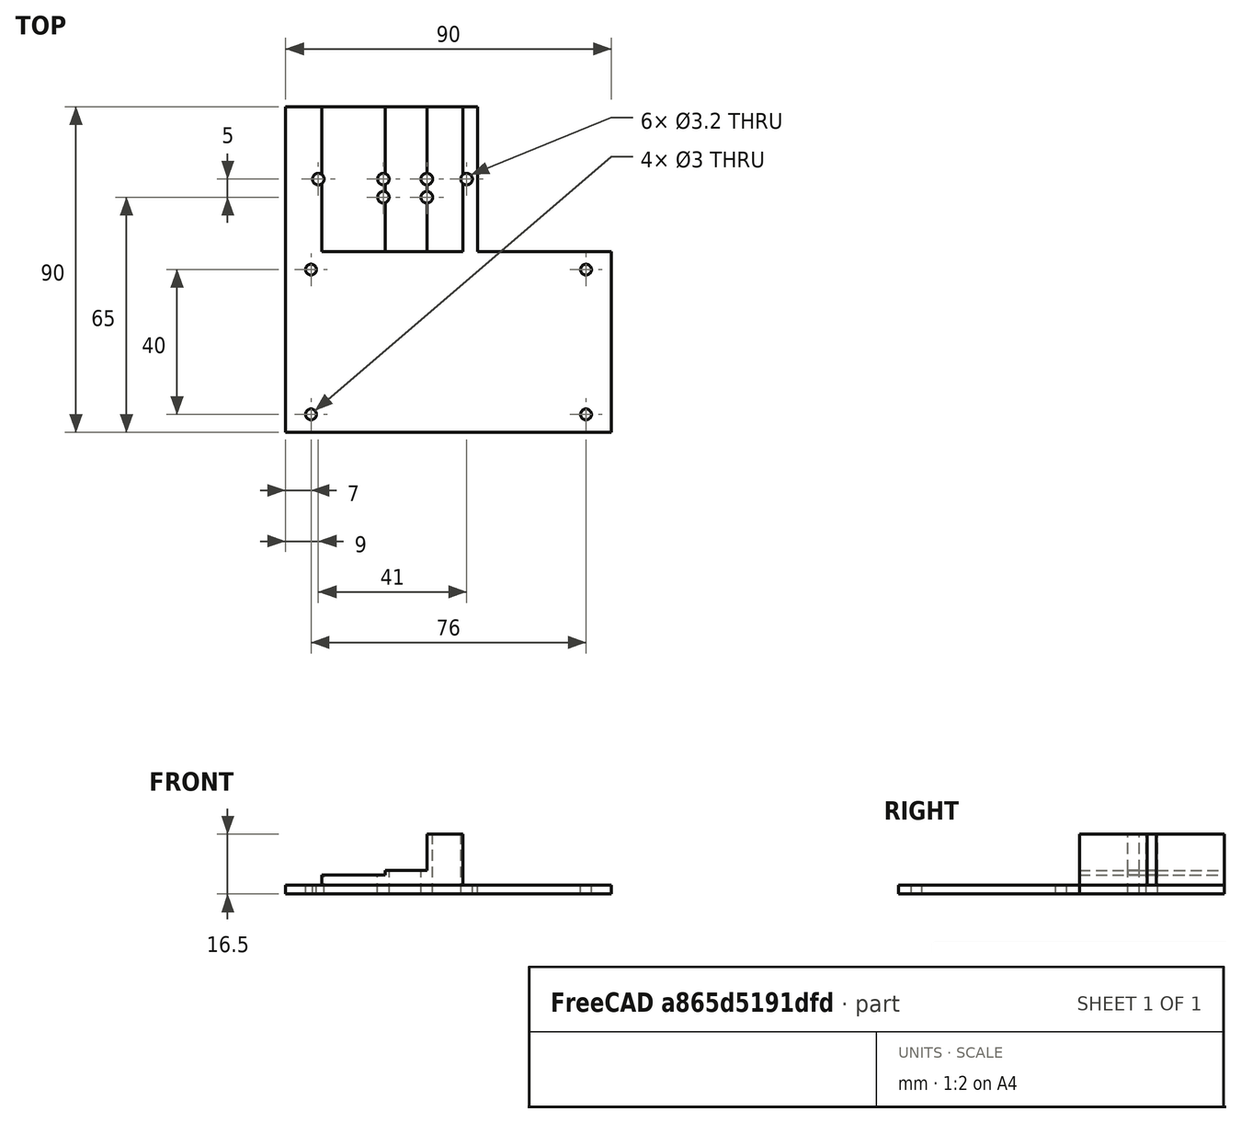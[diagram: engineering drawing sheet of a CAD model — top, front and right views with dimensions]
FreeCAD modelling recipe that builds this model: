
FCSTD DOCUMENT  (FreeCAD 0.16R6707 (Git))
Label: U3-base
License: All rights reserved
LicenseURL: http://en.wikipedia.org/wiki/All_rights_reserved
objects: Part::Cut×11, Part::Cylinder×10, Part::Box×5, Part::MultiFuse×3
note: 29 computed .brp shape members not serialized (recipe doc carries the construction recipe); baked Part::Feature solids carry a one-line shape summary decoded from their .brp

FEATURE [Part::Box] Box  label="Cube"
  Height = 2.5
  Length = 90
  Placement = pos=(0,0,-2.5) rot=(0,0,1;0rad)
  Width = 90
FEATURE [Part::Cylinder] Cylinder
  Angle = 360
  Height = 10
  Placement = pos=(7,5,-5) rot=(0,0,1;0rad)
  Radius = 1.5
FEATURE [Part::Cylinder] Cylinder001
  Angle = 360
  Height = 10
  Placement = pos=(7,45,-5) rot=(0,0,1;0rad)
  Radius = 1.5
FEATURE [Part::Cylinder] Cylinder002
  Angle = 360
  Height = 10
  Placement = pos=(83,5,-5) rot=(0,0,1;0rad)
  Radius = 1.5
FEATURE [Part::Cylinder] Cylinder003
  Angle = 360
  Height = 10
  Placement = pos=(83,45,-5) rot=(0,0,1;0rad)
  Radius = 1.5
FEATURE [Part::Box] Box001  label="Cube001"
  Height = 2.75
  Length = 17.5
  Placement = pos=(10,50,0) rot=(0,0,1;0rad)
  Width = 40
FEATURE [Part::Box] Box002  label="Cube002"
  Height = 4
  Length = 11.5
  Placement = pos=(27.5,50,0) rot=(0,0,1;0rad)
  Width = 40
FEATURE [Part::Cylinder] Cylinder004
  Angle = 360
  Height = 10
  Placement = pos=(9,70,-5) rot=(0,0,1;0rad)
  Radius = 1.6
FEATURE [Part::Cylinder] Cylinder005
  Angle = 360
  Height = 10
  Placement = pos=(27,70,-5) rot=(0,0,1;0rad)
  Radius = 1.6
FEATURE [Part::Cylinder] Cylinder006
  Angle = 360
  Height = 10
  Placement = pos=(27,65,-5) rot=(0,0,1;0rad)
  Radius = 1.6
FEATURE [Part::Cylinder] Cylinder007
  Angle = 360
  Height = 20
  Placement = pos=(39,65,-5) rot=(0,0,1;0rad)
  Radius = 1.6
FEATURE [Part::Box] Box003  label="Cube003"
  Height = 14
  Length = 10
  Placement = pos=(39,50,0) rot=(0,0,1;0rad)
  Width = 40
FEATURE [Part::Cylinder] Cylinder008
  Angle = 360
  Height = 20
  Placement = pos=(39,70,-5) rot=(0,0,1;0rad)
  Radius = 1.6
FEATURE [Part::Cylinder] Cylinder009
  Angle = 360
  Height = 20
  Placement = pos=(50,70,-5) rot=(0,0,1;0rad)
  Radius = 1.6
FEATURE [Part::Cut] Cut
  Base = -> Box
  Tool = -> Cylinder
FEATURE [Part::Cut] Cut001
  Base = -> Cut
  Tool = -> Cylinder001
FEATURE [Part::Cut] Cut002
  Base = -> Cut001
  Tool = -> Cylinder002
FEATURE [Part::Cut] Cut003
  Base = -> Cut002
  Tool = -> Cylinder003
FEATURE [Part::MultiFuse] Fusion
  Shapes = -> [Cut003,Box001]
FEATURE [Part::MultiFuse] Fusion001
  Shapes = -> [Fusion,Box002]
FEATURE [Part::MultiFuse] Fusion002
  Shapes = -> [Fusion001,Box003]
FEATURE [Part::Cut] Cut004
  Base = -> Fusion002
  Tool = -> Cylinder004
FEATURE [Part::Cut] Cut005
  Base = -> Cut004
  Tool = -> Cylinder005
FEATURE [Part::Cut] Cut006
  Base = -> Cut005
  Tool = -> Cylinder006
FEATURE [Part::Cut] Cut007
  Base = -> Cut006
  Tool = -> Cylinder007
FEATURE [Part::Cut] Cut008
  Base = -> Cut007
  Tool = -> Cylinder008
FEATURE [Part::Cut] Cut009
  Base = -> Cut008
  Tool = -> Cylinder009
FEATURE [Part::Box] Box004  label="Cube004"
  Height = 10
  Length = 40
  Placement = pos=(53,50,-5) rot=(0,0,1;0rad)
  Width = 40
FEATURE [Part::Cut] Cut010
  Base = -> Cut009
  Tool = -> Box004
